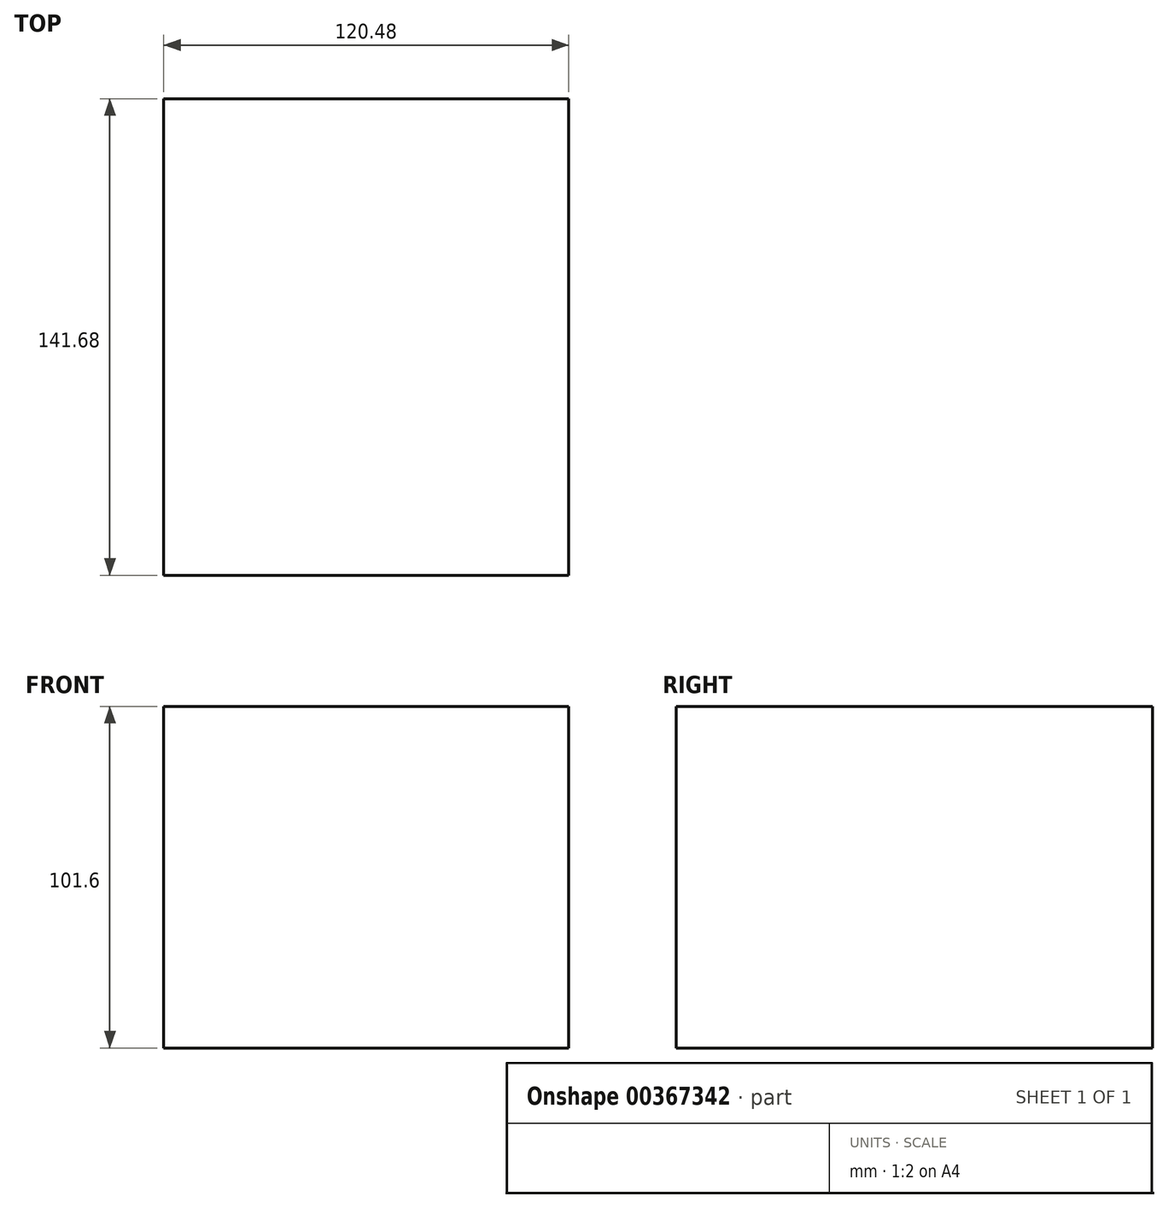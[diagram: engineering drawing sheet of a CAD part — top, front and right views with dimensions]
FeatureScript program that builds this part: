
annotation { "Feature Type Name" : "Feature", "Feature Type Description" : "" }
export const myFeature = defineFeature(function(context is Context, id is Id, definition is map)
    precondition{}
    {
        {
            var Q0;
            Q0=qCreatedBy(makeId("Top.planeOp"),FACE);
            var sketch = newSketch(context, id + "F0", { "sketchPlane" : qUnion([Q0])});
            skLineSegment(sketch, "E0.bottom", {"start": v(0, 70.84) * mm, "end": v(120.48, 70.84) * mm});
            skLineSegment(sketch, "E0.top", {"start": v(0, -70.84) * mm, "end": v(120.48, -70.84) * mm});
            skLineSegment(sketch, "E0.left", {"start": v(0, 70.84) * mm, "end": v(0, -70.84) * mm});
            skLineSegment(sketch, "E0.right", {"start": v(120.48, 70.84) * mm, "end": v(120.48, -70.84) * mm});
            skPoint(sketch, "E0.middle", {"position": v(60.24, 0) * mm});
            skSolve(sketch);
        }
        {
            var Q0;
            Q0=makeQuery(id+"F0.imprint","IMPRINT",FACE,{"disambiguationData":[TD([[makeQuery(id+"F0.imprint","IMPRINT",EDGE,{"derivedFrom":sQuery(id+"F0.wireOp",EDGE,"E0.bottom")}),-1.0]])]});
            extrude(context, id + "F1", {"entities" : qUnion([Q0]), "depth" : 101.6 * mm});
        }
    });
